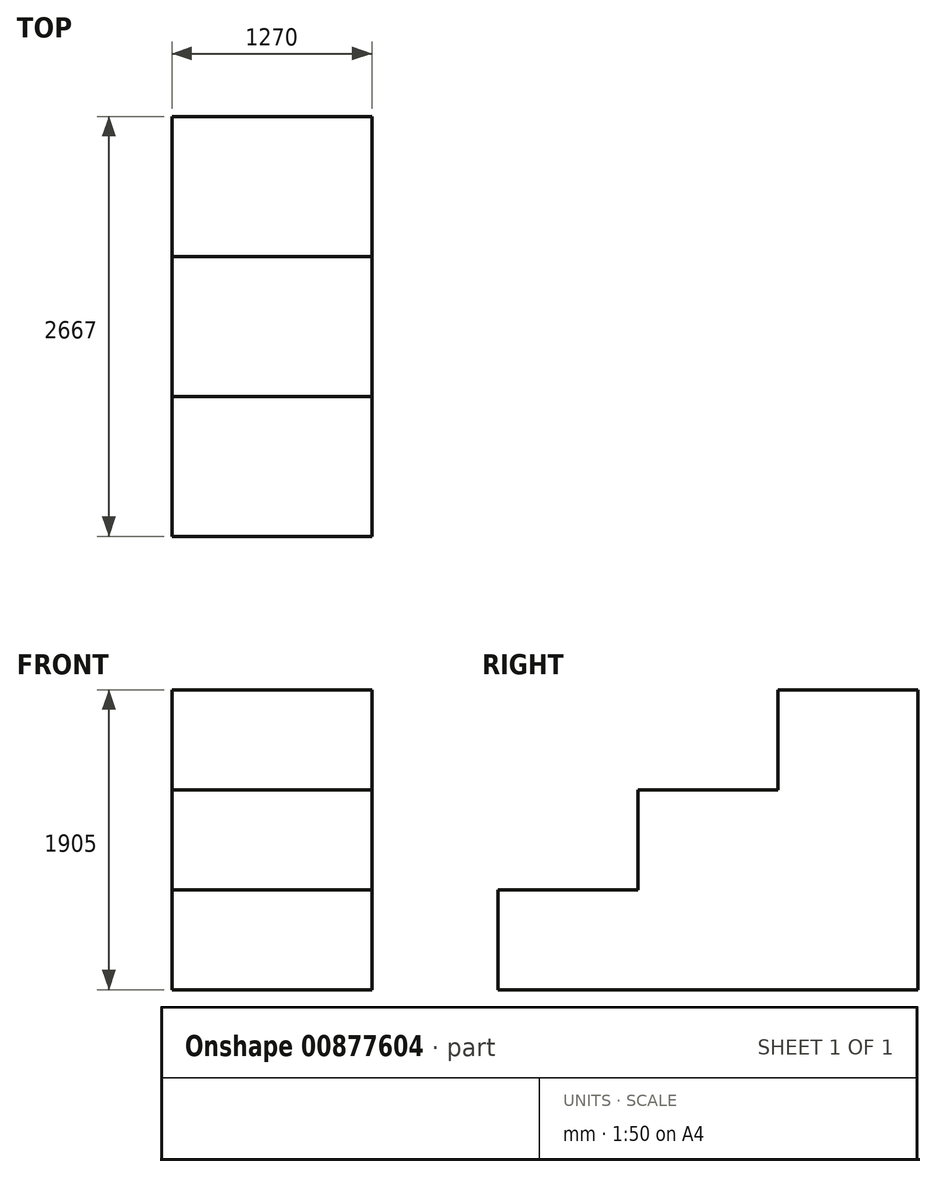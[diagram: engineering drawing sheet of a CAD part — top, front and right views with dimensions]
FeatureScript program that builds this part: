
annotation { "Feature Type Name" : "Feature", "Feature Type Description" : "" }
export const myFeature = defineFeature(function(context is Context, id is Id, definition is map)
    precondition{}
    {
        {
            var Q0;
            Q0=qCreatedBy(makeId("Right.planeOp"),FACE);
            var sketch = newSketch(context, id + "F0", { "sketchPlane" : qUnion([Q0])});
            skLineSegment(sketch, "E0", {"start": v(0, 0) * mm, "end": v(-2667, 0) * mm});
            skLineSegment(sketch, "E1", {"start": v(-2667, 0) * mm, "end": v(-2667, 635) * mm});
            skLineSegment(sketch, "E2", {"start": v(-2667, 635) * mm, "end": v(-1778, 635) * mm});
            skLineSegment(sketch, "E3", {"start": v(-1778, 635) * mm, "end": v(-1778, 1270) * mm});
            skLineSegment(sketch, "E4", {"start": v(-1778, 1270) * mm, "end": v(-889, 1270) * mm});
            skLineSegment(sketch, "E5", {"start": v(-889, 1270) * mm, "end": v(-889, 1905) * mm});
            skLineSegment(sketch, "E6", {"start": v(-889, 1905) * mm, "end": v(0, 1905) * mm});
            skLineSegment(sketch, "E7", {"start": v(0, 1905) * mm, "end": v(0, 0) * mm});
            skSolve(sketch);
        }
        {
            var Q0;
            Q0=qSketchRegion(id+"F0",true);
            extrude(context, id + "F1", {"entities" : qUnion([Q0]), "oppositeDirection" : true, "depth" : 1270 * mm, "offsetDistance" : 25.4 * mm});
        }
    });
